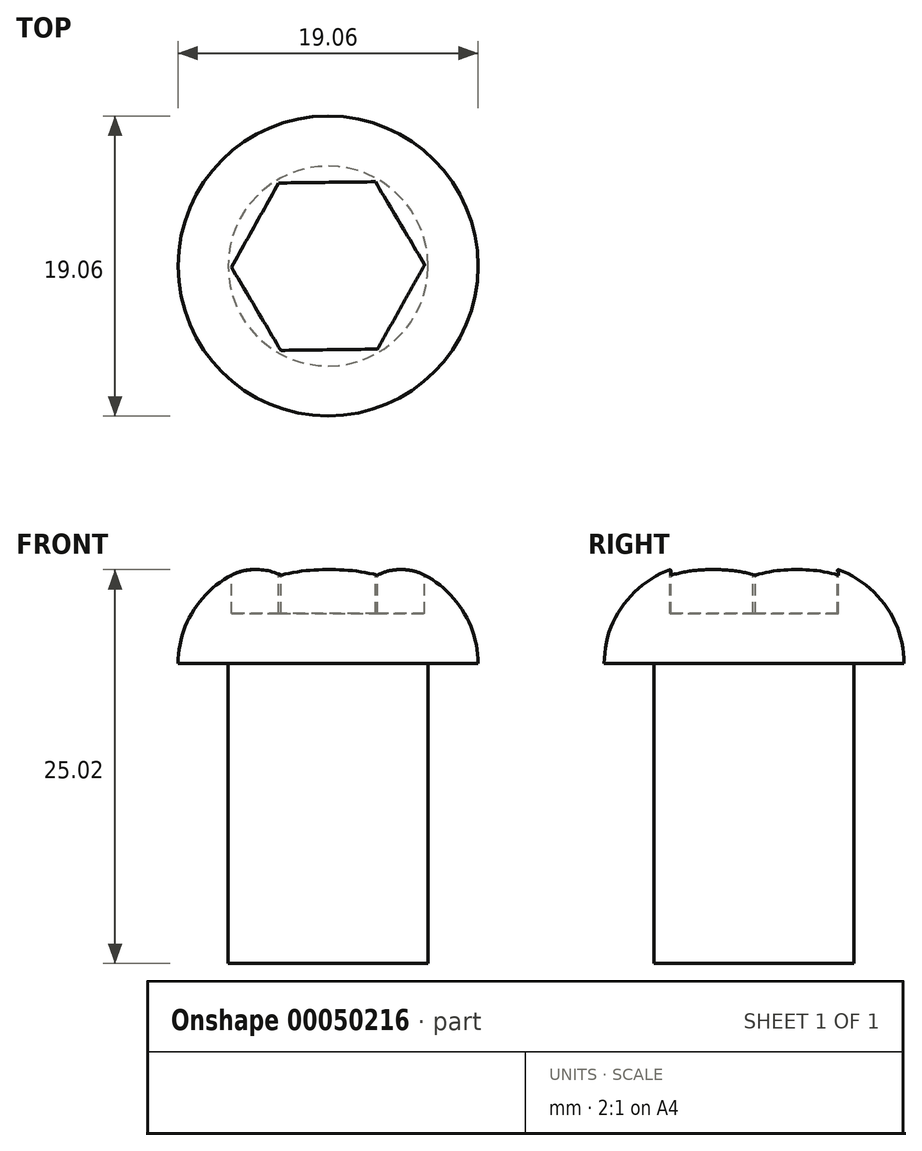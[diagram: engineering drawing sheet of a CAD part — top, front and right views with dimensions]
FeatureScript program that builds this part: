
annotation { "Feature Type Name" : "Feature", "Feature Type Description" : "" }
export const myFeature = defineFeature(function(context is Context, id is Id, definition is map)
    precondition{}
    {
        {
            var Q0;
            Q0=qCreatedBy(makeId("Front.planeOp"),FACE);
            var sketch = newSketch(context, id + "F0", { "sketchPlane" : qUnion([Q0])});
            skLineSegment(sketch, "E0", {"start": v(0, 17.84) * mm, "end": v(9.53, 17.84) * mm});
            skLineSegment(sketch, "E1", {"start": v(9.53, 17.84) * mm, "end": v(9.53, 11.49) * mm});
            skLineSegment(sketch, "E2", {"start": v(9.53, 11.49) * mm, "end": v(6.35, 11.49) * mm});
            skLineSegment(sketch, "E3", {"start": v(6.35, 11.49) * mm, "end": v(6.35, -7.56) * mm});
            skLineSegment(sketch, "E4", {"start": v(6.35, -7.56) * mm, "end": v(0, -7.56) * mm});
            skLineSegment(sketch, "E5", {"start": v(0, 45.5) * mm, "end": v(0, -39.5) * mm, "construction": true});
            skLineSegment(sketch, "E6", {"start": v(0, -7.56) * mm, "end": v(0, 17.84) * mm});
            skSolve(sketch);
        }
        {
            var Q0;
            Q0=qSketchRegion(id+"F0",true);
            var Q1;
            Q1=sQuery(id+"F0.wireOp",EDGE,"E5");
            revolve(context, id + "F1", {"entities" : qUnion([Q0]), "axis" : qUnion([Q1]), "revolveType" : RevolveType.FULL});
        }
        {
            var Q0;
            Q0=makeQuery(id+"F1.opRevolve","SWEPT_FACE",FACE,{"disambiguationData":[OSD([sQuery(id+"F0.wireOp",EDGE,"E0")])]});
            var sketch = newSketch(context, id + "F2", { "sketchPlane" : qUnion([Q0])});
            skCircle(sketch, "E7.cCircle", {"center": v(0, 0) * mm, "radius": 6.14 * mm, "construction": true});
            skLineSegment(sketch, "E7.0", {"start": v(3.14, -5.28) * mm, "end": v(-3, -5.36) * mm});
            skLineSegment(sketch, "E7.1", {"start": v(-3, -5.36) * mm, "end": v(-6.14, -0.08) * mm});
            skLineSegment(sketch, "E7.2", {"start": v(-6.14, -0.08) * mm, "end": v(-3.14, 5.28) * mm});
            skLineSegment(sketch, "E7.3", {"start": v(-3.14, 5.28) * mm, "end": v(3, 5.36) * mm});
            skLineSegment(sketch, "E7.4", {"start": v(3, 5.36) * mm, "end": v(6.14, 0.08) * mm});
            skLineSegment(sketch, "E7.5", {"start": v(6.14, 0.08) * mm, "end": v(3.14, -5.28) * mm});
            skSolve(sketch);
        }
        {
            var Q0;
            Q0=qSketchRegion(id+"F2",true);
            extrude(context, id + "F3", {"entities" : qUnion([Q0]), "operationType" : NewBodyOperationType.REMOVE, "oppositeDirection" : true, "depth" : 3.17 * mm});
        }
        {
            var Q0;
            Q0=makeQuery(id+"F1.opRevolve","SWEPT_EDGE",EDGE,{"disambiguationData":[OSD([sQuery(id+"F0.wireOp",EDGE,"E0"),sQuery(id+"F0.wireOp",EDGE,"E1")])]});
            fillet(context, id + "F4", {"entities" : qUnion([Q0]), "radius" : 6.35 * mm, "tangentPropagation" : true, "allowEdgeOverflow" : false});
        }
    });
